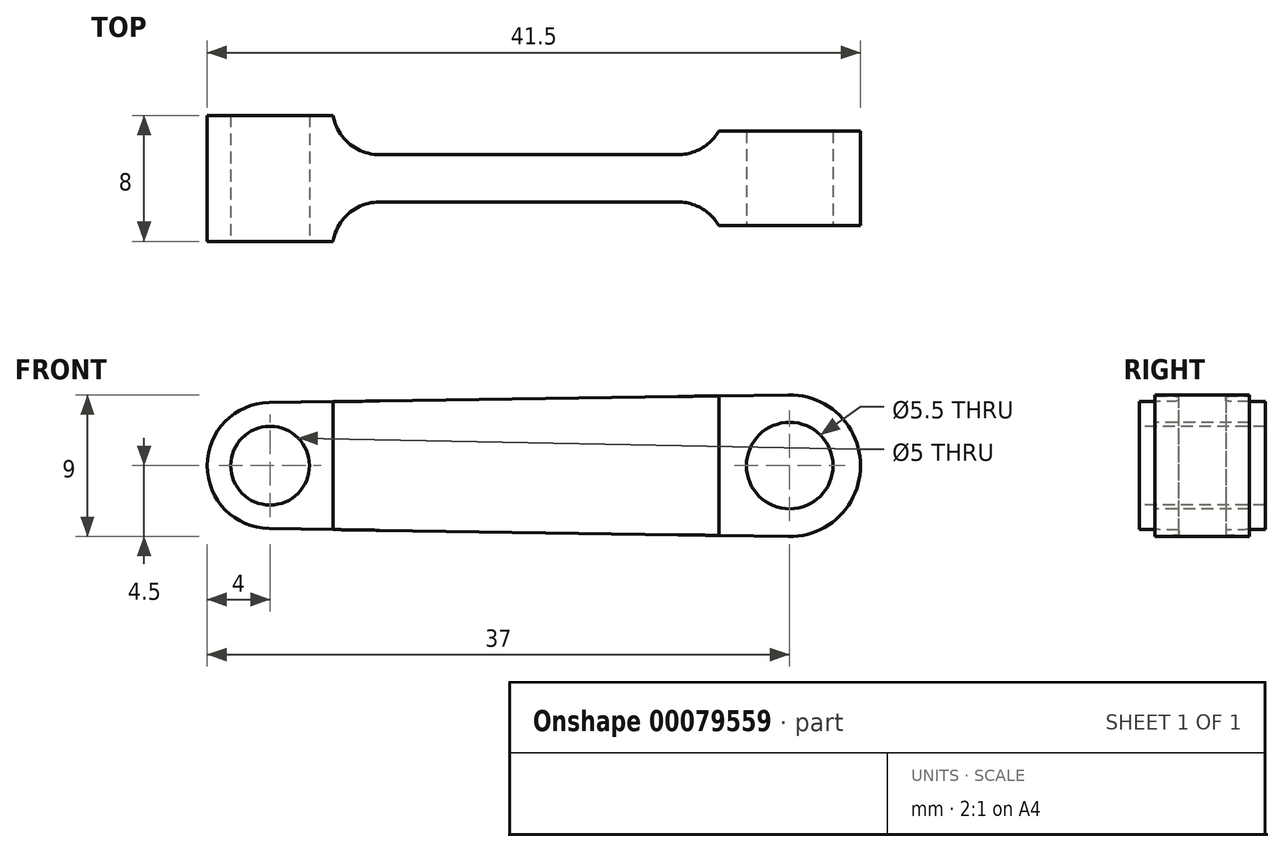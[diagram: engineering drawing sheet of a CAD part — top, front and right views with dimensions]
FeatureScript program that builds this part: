
annotation { "Feature Type Name" : "Feature", "Feature Type Description" : "" }
export const myFeature = defineFeature(function(context is Context, id is Id, definition is map)
    precondition{}
    {
        {
            var Q0;
            Q0=qCreatedBy(makeId("Front.planeOp"),FACE);
            var sketch = newSketch(context, id + "F0", { "sketchPlane" : qUnion([Q0])});
            skArc(sketch, "E0", {"start": v(-16.56, 4) * mm, "mid": v(-20.5, 0) * mm, "end": v(-16.56, -4) * mm});
            skArc(sketch, "E1", {"start": v(16.43, -4.5) * mm, "mid": v(21, 0) * mm, "end": v(16.43, 4.5) * mm});
            skLineSegment(sketch, "E2", {"start": v(-16.56, -4) * mm, "end": v(16.43, -4.5) * mm});
            skLineSegment(sketch, "E3", {"start": v(-16.56, 4) * mm, "end": v(16.43, 4.5) * mm});
            skSolve(sketch);
        }
        {
            var Q0;
            Q0=makeQuery(id+"F0.imprint","IMPRINT",FACE,{"disambiguationData":[TD([[makeQuery(id+"F0.imprint","IMPRINT",EDGE,{"derivedFrom":sQuery(id+"F0.wireOp",EDGE,"E0")}),1.0]])]});
            extrude(context, id + "F1", {"entities" : qUnion([Q0]), "depth" : 1.5 * mm, "hasSecondDirection" : true, "secondDirectionOppositeDirection" : true, "secondDirectionDepth" : 1.5 * mm});
        }
        {
            var Q0;
            Q0=qCreatedBy(makeId("Front.planeOp"),FACE);
            var sketch = newSketch(context, id + "F2", { "sketchPlane" : qUnion([Q0])});
            skLineSegment(sketch, "E4.0", {"start": v(-16.56, 4) * mm, "end": v(-12.5, 4.06) * mm});
            skArc(sketch, "E5.0", {"start": v(-16.56, 4) * mm, "mid": v(-20.5, 0) * mm, "end": v(-16.56, -4) * mm});
            skLineSegment(sketch, "E6.0", {"start": v(-16.56, -4) * mm, "end": v(-12.5, -4.06) * mm});
            skLineSegment(sketch, "E7", {"start": v(-12.5, 4.06) * mm, "end": v(-12.5, -4.06) * mm});
            skPoint(sketch, "E8.0.end.orphan", {"position": v(16.43, 4.5) * mm});
            skPoint(sketch, "E8.0.start.orphan", {"position": v(16.43, -4.5) * mm});
            skSolve(sketch);
        }
        {
            var Q0;
            Q0 = qSketchRegion(id + "F2", true);
            extrude(context, id + "F3", {"entities" : qUnion([Q0]), "operationType" : NewBodyOperationType.ADD, "depth" : 4 * mm, "hasSecondDirection" : true, "secondDirectionOppositeDirection" : true, "secondDirectionDepth" : 4 * mm});
        }
        {
            var Q0;
            Q0=qCreatedBy(makeId("Front.planeOp"),FACE);
            var sketch = newSketch(context, id + "F4", { "sketchPlane" : qUnion([Q0])});
            skLineSegment(sketch, "E9.0", {"start": v(12, 4.43) * mm, "end": v(16.43, 4.5) * mm});
            skLineSegment(sketch, "E10.0", {"start": v(12, -4.43) * mm, "end": v(16.43, -4.5) * mm});
            skArc(sketch, "E11.0", {"start": v(16.43, -4.5) * mm, "mid": v(21, 0) * mm, "end": v(16.43, 4.5) * mm});
            skLineSegment(sketch, "E12", {"start": v(12, 4.43) * mm, "end": v(12, -4.43) * mm});
            skPoint(sketch, "E13.orphan", {"position": v(-12.5, 4.06) * mm});
            skPoint(sketch, "E14.orphan", {"position": v(-12.5, -4.06) * mm});
            skSolve(sketch);
        }
        {
            var Q0;
            Q0 = qSketchRegion(id + "F4", true);
            extrude(context, id + "F5", {"entities" : qUnion([Q0]), "operationType" : NewBodyOperationType.ADD, "depth" : 3 * mm, "hasSecondDirection" : true, "secondDirectionOppositeDirection" : true, "secondDirectionDepth" : 3 * mm});
        }
        {
            var Q0;
            Q0=qCreatedBy(makeId("Front.planeOp"),FACE);
            var sketch = newSketch(context, id + "F6", { "sketchPlane" : qUnion([Q0])});
            skCircle(sketch, "E15", {"center": v(-16.5, 0) * mm, "radius": 2.5 * mm});
            skCircle(sketch, "E16", {"center": v(16.5, 0) * mm, "radius": 2.75 * mm});
            skPoint(sketch, "E17.0.end.orphan", {"position": v(-16.56, -4) * mm});
            skPoint(sketch, "E17.0.start.orphan", {"position": v(-16.56, 4) * mm});
            skPoint(sketch, "E18.0.end.orphan", {"position": v(16.43, 4.5) * mm});
            skPoint(sketch, "E18.0.start.orphan", {"position": v(16.43, -4.5) * mm});
            skSolve(sketch);
        }
        {
            var Q0;
            Q0 = qSketchRegion(id + "F6", true);
            extrude(context, id + "F7", {"entities" : qUnion([Q0]), "operationType" : NewBodyOperationType.REMOVE, "endBound" : BoundingType.THROUGH_ALL, "oppositeDirection" : true, "depth" : 25 * mm, "hasSecondDirection" : true, "secondDirectionBound" : SecondDirectionBoundingType.THROUGH_ALL, "secondDirectionOppositeDirection" : false, "secondDirectionDepth" : 25 * mm});
        }
        {
            var Q0;
            Q0=makeQuery(id+"F3.boolean.opBoolean","INTERSECT",EDGE,{"derivedFrom":[makeQuery(id+"F1.opExtrude","CAP_FACE",FACE,{"disambiguationData":[OSD([sQuery(id+"F0.wireOp",EDGE,"E0"),sQuery(id+"F0.wireOp",EDGE,"E1"),sQuery(id+"F0.wireOp",EDGE,"E2"),sQuery(id+"F0.wireOp",EDGE,"E3")])],"isStart":false}),makeQuery(id+"F3.opExtrude","SWEPT_FACE",FACE,{"disambiguationData":[OSD([sQuery(id+"F2.wireOp",EDGE,"E7")])]})]});
            var Q1;
            Q1=makeQuery(id+"F5.boolean.opBoolean","INTERSECT",EDGE,{"derivedFrom":[makeQuery(id+"F1.opExtrude","CAP_FACE",FACE,{"disambiguationData":[OSD([sQuery(id+"F0.wireOp",EDGE,"E0"),sQuery(id+"F0.wireOp",EDGE,"E1"),sQuery(id+"F0.wireOp",EDGE,"E2"),sQuery(id+"F0.wireOp",EDGE,"E3")])],"isStart":false}),makeQuery(id+"F5.opExtrude","SWEPT_FACE",FACE,{"disambiguationData":[OSD([sQuery(id+"F4.wireOp",EDGE,"E12")])]})]});
            var Q2;
            Q2=makeQuery(id+"F5.boolean.opBoolean","INTERSECT",EDGE,{"derivedFrom":[makeQuery(id+"F1.opExtrude","CAP_FACE",FACE,{"disambiguationData":[OSD([sQuery(id+"F0.wireOp",EDGE,"E0"),sQuery(id+"F0.wireOp",EDGE,"E1"),sQuery(id+"F0.wireOp",EDGE,"E2"),sQuery(id+"F0.wireOp",EDGE,"E3")])],"isStart":true}),makeQuery(id+"F5.opExtrude","SWEPT_FACE",FACE,{"disambiguationData":[OSD([sQuery(id+"F4.wireOp",EDGE,"E12")])]})]});
            var Q3;
            Q3=makeQuery(id+"F3.boolean.opBoolean","INTERSECT",EDGE,{"derivedFrom":[makeQuery(id+"F1.opExtrude","CAP_FACE",FACE,{"disambiguationData":[OSD([sQuery(id+"F0.wireOp",EDGE,"E0"),sQuery(id+"F0.wireOp",EDGE,"E1"),sQuery(id+"F0.wireOp",EDGE,"E2"),sQuery(id+"F0.wireOp",EDGE,"E3")])],"isStart":true}),makeQuery(id+"F3.opExtrude","SWEPT_FACE",FACE,{"disambiguationData":[OSD([sQuery(id+"F2.wireOp",EDGE,"E7")])]})]});
            fillet(context, id + "F8", {"entities" : qUnion([Q0, Q1, Q2, Q3]), "radius" : 3 * mm, "tangentPropagation" : true, "allowEdgeOverflow" : false});
        }
        {
            var Q0;
            Q0=makeQuery(id+"F5.boolean.opBoolean","MERGE",FACE,{"derivedFrom":[makeQuery(id+"F1.opExtrude","SWEPT_FACE",FACE,{"disambiguationData":[OSD([sQuery(id+"F0.wireOp",EDGE,"E1")])]}),makeQuery(id+"F5.opExtrude","SWEPT_FACE",FACE,{"disambiguationData":[OSD([sQuery(id+"F4.wireOp",EDGE,"E11.0")])]})]});
            cPlane(context, id + "F9", {"entities" : qUnion([Q0]), "cplaneType" : CPlaneType.LINE_ANGLE, "offset" : 150 * mm, "angle" : 45 * degree, "width" : 150 * mm, "height" : 150 * mm});
        }
        {
            var Q0;
            Q0=qCreatedBy(id+"F9.planeOp",FACE);
            var sketch = newSketch(context, id + "F10", { "sketchPlane" : qUnion([Q0])});
            skCircle(sketch, "E19", {"center": v(11.67, 0) * mm, "radius": 1 * mm});
            skPoint(sketch, "E20.trimOffspring.end.orphan", {"position": v(11.67, 3) * mm});
            skPoint(sketch, "E21.orphan", {"position": v(8.92, 3) * mm});
            skPoint(sketch, "E22.0.start.orphan", {"position": v(14.42, 3) * mm});
            skPoint(sketch, "E23.start.orphan", {"position": v(11.67, -3) * mm});
            skPoint(sketch, "E24.orphan", {"position": v(14.42, -3) * mm});
            skPoint(sketch, "E25.0.end.orphan", {"position": v(8.92, -3) * mm});
            skSolve(sketch);
        }
        {
            var Q0;
            Q0 = qSketchRegion(id + "F10", true);
            extrude(context, id + "F11", {"entities" : qUnion([Q0]), "operationType" : NewBodyOperationType.REMOVE, "endBound" : BoundingType.THROUGH_ALL, "depth" : 25 * mm});
        }
    });
